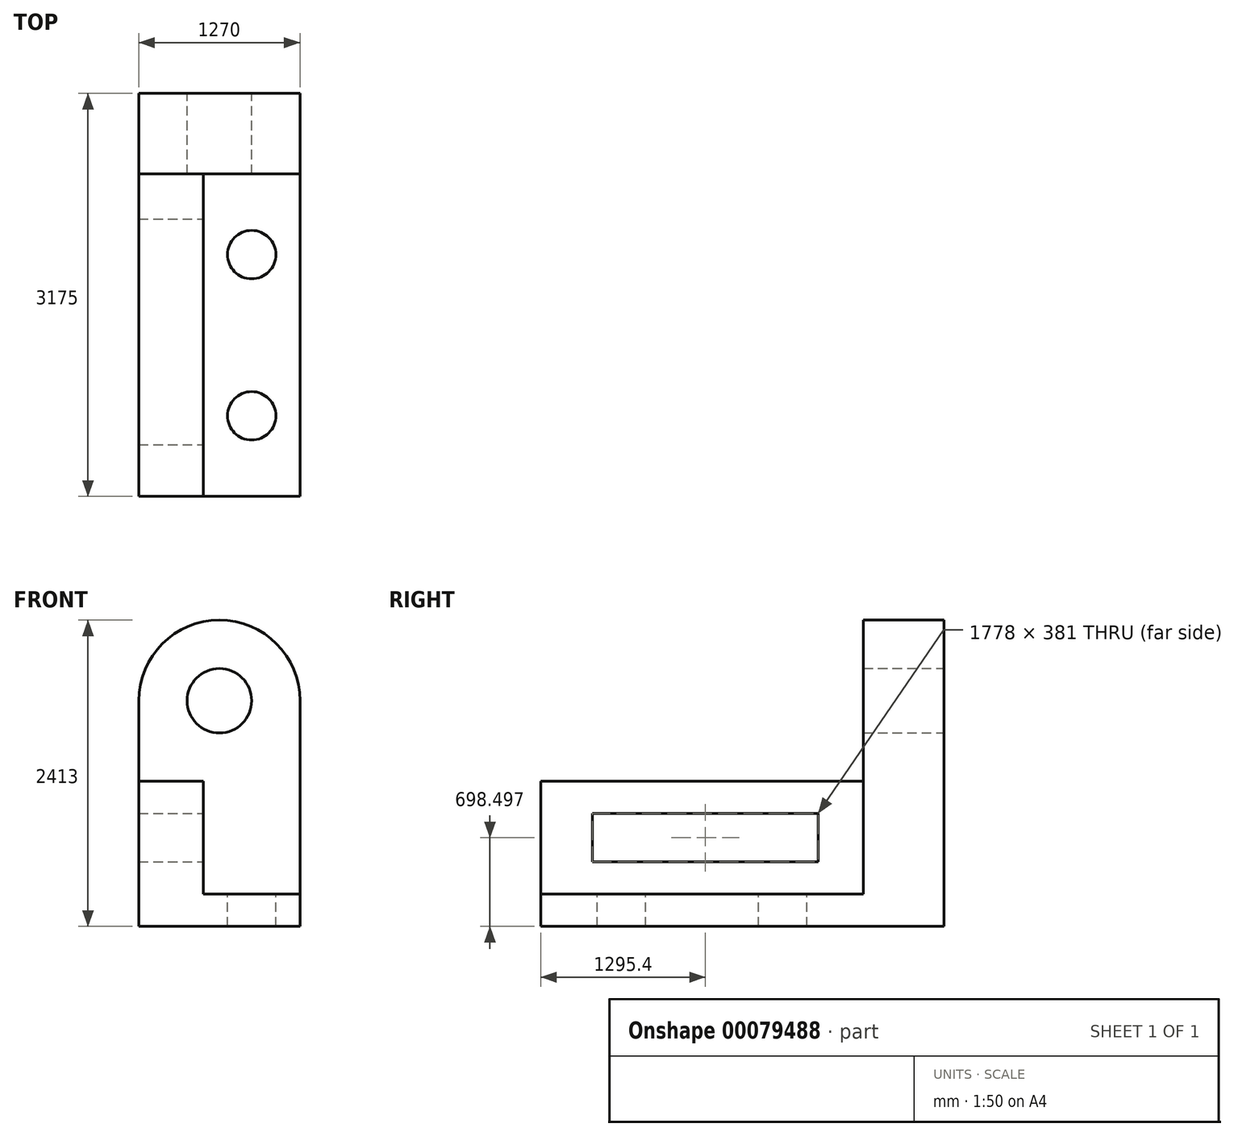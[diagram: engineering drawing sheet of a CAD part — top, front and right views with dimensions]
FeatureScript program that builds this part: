
annotation { "Feature Type Name" : "Feature", "Feature Type Description" : "" }
export const myFeature = defineFeature(function(context is Context, id is Id, definition is map)
    precondition{}
    {
        {
            var Q0;
            Q0=qCreatedBy(makeId("Right.planeOp"),FACE);
            var sketch = newSketch(context, id + "F0", { "sketchPlane" : qUnion([Q0])});
            skLineSegment(sketch, "E0", {"start": v(-1055.67, 9.56) * mm, "end": v(-1055.67, -244.44) * mm});
            skLineSegment(sketch, "E1", {"start": v(-1055.67, -244.44) * mm, "end": v(1484.33, -244.44) * mm});
            skLineSegment(sketch, "E2", {"start": v(1484.33, -244.44) * mm, "end": v(1484.33, 9.56) * mm});
            skLineSegment(sketch, "E3", {"start": v(1484.33, 9.56) * mm, "end": v(-1055.67, 9.56) * mm});
            skSolve(sketch);
        }
        {
            var Q0;
            Q0=makeQuery(id+"F0.imprint","IMPRINT",FACE,{"disambiguationData":[TD([[makeQuery(id+"F0.imprint","IMPRINT",EDGE,{"derivedFrom":sQuery(id+"F0.wireOp",EDGE,"E0")}),1.0]])]});
            extrude(context, id + "F1", {"entities" : qUnion([Q0]), "depth" : 1270 * mm});
        }
        {
            var Q0;
            Q0=makeQuery(id+"F1.opExtrude","SWEPT_FACE",FACE,{"disambiguationData":[OSD([sQuery(id+"F0.wireOp",EDGE,"E2")])]});
            var sketch = newSketch(context, id + "F2", { "sketchPlane" : qUnion([Q0])});
            skArc(sketch, "E4", {"start": v(0, 1533.56) * mm, "mid": v(-635, 2168.56) * mm, "end": v(-1270, 1533.56) * mm});
            skLineSegment(sketch, "E5", {"start": v(-1270, 1533.56) * mm, "end": v(-1270, 9.56) * mm});
            skLineSegment(sketch, "E6", {"start": v(0, 1533.56) * mm, "end": v(0, 9.56) * mm});
            skLineSegment(sketch, "E7", {"start": v(-1270, 9.56) * mm, "end": v(-1270, -244.44) * mm});
            skLineSegment(sketch, "E8", {"start": v(-1270, -244.44) * mm, "end": v(0, -244.44) * mm});
            skLineSegment(sketch, "E9", {"start": v(0, -244.44) * mm, "end": v(0, 9.56) * mm});
            skSolve(sketch);
        }
        {
            var Q0;
            Q0 = qSketchRegion(id + "F2", true);
            extrude(context, id + "F3", {"entities" : qUnion([Q0]), "operationType" : NewBodyOperationType.ADD, "depth" : 635 * mm});
        }
        {
            var Q0;
            Q0=makeQuery(id+"F3.opExtrude","CAP_FACE",FACE,{"disambiguationData":[OSD([sQuery(id+"F2.wireOp",EDGE,"E4"),sQuery(id+"F2.wireOp",EDGE,"E5"),sQuery(id+"F2.wireOp",EDGE,"E6"),sQuery(id+"F2.wireOp",EDGE,"E7"),sQuery(id+"F2.wireOp",EDGE,"E8"),sQuery(id+"F2.wireOp",EDGE,"E9")])],"isStart":false});
            var sketch = newSketch(context, id + "F4", { "sketchPlane" : qUnion([Q0])});
            skPoint(sketch, "E10", {"position": v(-635, 1533.56) * mm});
            skSolve(sketch);
        }
        {
            var Q0;
            Q0=sQuery(id+"F4.wireOp",VERTEX,"E10");
            var Q1;
            Q1=makeQuery(id+"F1.opExtrude","SWEPT_BODY",BODY,{"disambiguationData":[OSD([sQuery(id+"F0.wireOp",EDGE,"E0"),sQuery(id+"F0.wireOp",EDGE,"E1"),sQuery(id+"F0.wireOp",EDGE,"E2"),sQuery(id+"F0.wireOp",EDGE,"E3")])]});
            hole(context, id + "F5", {"style" : HoleStyle.SIMPLE, "endStyle" : HoleEndStyle.THROUGH, "holeDiameter" : 508 * mm, "locations" : qUnion([Q0]), "scope" : qUnion([Q1]), "isTappedThrough" : true});
        }
        {
            var Q0;
            Q0=makeQuery(id+"F1.opExtrude","SWEPT_FACE",FACE,{"disambiguationData":[OSD([sQuery(id+"F0.wireOp",EDGE,"E3")])]});
            var sketch = newSketch(context, id + "F6", { "sketchPlane" : qUnion([Q0])});
            skLineSegment(sketch, "E11", {"start": v(0, -1055.67) * mm, "end": v(508, -1055.67) * mm});
            skLineSegment(sketch, "E12", {"start": v(508, -1055.67) * mm, "end": v(508, 1484.33) * mm});
            skLineSegment(sketch, "E13", {"start": v(508, 1484.33) * mm, "end": v(0, 1484.33) * mm});
            skLineSegment(sketch, "E14", {"start": v(0, 1484.33) * mm, "end": v(0, -1055.67) * mm});
            skSolve(sketch);
        }
        {
            var Q0;
            Q0=makeQuery(id+"F6.imprint","IMPRINT",FACE,{"disambiguationData":[TD([[makeQuery(id+"F6.imprint","IMPRINT",EDGE,{"derivedFrom":sQuery(id+"F6.wireOp",EDGE,"E11")}),-1.0]])]});
            extrude(context, id + "F7", {"entities" : qUnion([Q0]), "operationType" : NewBodyOperationType.ADD, "depth" : 889 * mm});
        }
        {
            var Q0;
            Q0=makeQuery(id+"F7.opExtrude","SWEPT_FACE",FACE,{"disambiguationData":[OSD([sQuery(id+"F6.wireOp",EDGE,"E12")])]});
            var sketch = newSketch(context, id + "F8", { "sketchPlane" : qUnion([Q0])});
            skLineSegment(sketch, "E15.bottom", {"start": v(-649.27, 644.56) * mm, "end": v(1128.73, 644.56) * mm});
            skLineSegment(sketch, "E15.top", {"start": v(-649.27, 263.56) * mm, "end": v(1128.73, 263.56) * mm});
            skLineSegment(sketch, "E15.left", {"start": v(-649.27, 644.56) * mm, "end": v(-649.27, 263.56) * mm});
            skLineSegment(sketch, "E15.right", {"start": v(1128.73, 644.56) * mm, "end": v(1128.73, 263.56) * mm});
            skSolve(sketch);
        }
        {
            var Q0;
            Q0=makeQuery(id+"F8.imprint","IMPRINT",FACE,{"disambiguationData":[TD([[makeQuery(id+"F8.imprint","IMPRINT",EDGE,{"derivedFrom":sQuery(id+"F8.wireOp",EDGE,"E15.bottom")}),-1.0]])]});
            extrude(context, id + "F9", {"entities" : qUnion([Q0]), "operationType" : NewBodyOperationType.REMOVE, "oppositeDirection" : true, "depth" : 1565.87 * mm});
        }
        {
            var Q0;
            Q0=makeQuery(id+"F1.opExtrude","SWEPT_FACE",FACE,{"disambiguationData":[OSD([sQuery(id+"F0.wireOp",EDGE,"E3")])]});
            var sketch = newSketch(context, id + "F10", { "sketchPlane" : qUnion([Q0])});
            skPoint(sketch, "E16", {"position": v(889, -420.67) * mm});
            skPoint(sketch, "E17", {"position": v(889, 849.33) * mm});
            skSolve(sketch);
        }
        {
            var Q0;
            Q0=sQuery(id+"F10.wireOp",VERTEX,"E16");
            var Q1;
            Q1=sQuery(id+"F10.wireOp",VERTEX,"E17");
            var Q2;
            Q2=makeQuery(id+"F1.opExtrude","SWEPT_BODY",BODY,{"disambiguationData":[OSD([sQuery(id+"F0.wireOp",EDGE,"E0"),sQuery(id+"F0.wireOp",EDGE,"E1"),sQuery(id+"F0.wireOp",EDGE,"E2"),sQuery(id+"F0.wireOp",EDGE,"E3")])]});
            hole(context, id + "F11", {"style" : HoleStyle.SIMPLE, "endStyle" : HoleEndStyle.THROUGH, "holeDiameter" : 381 * mm, "locations" : qUnion([Q0, Q1]), "scope" : qUnion([Q2]), "isTappedThrough" : true});
        }
    });
